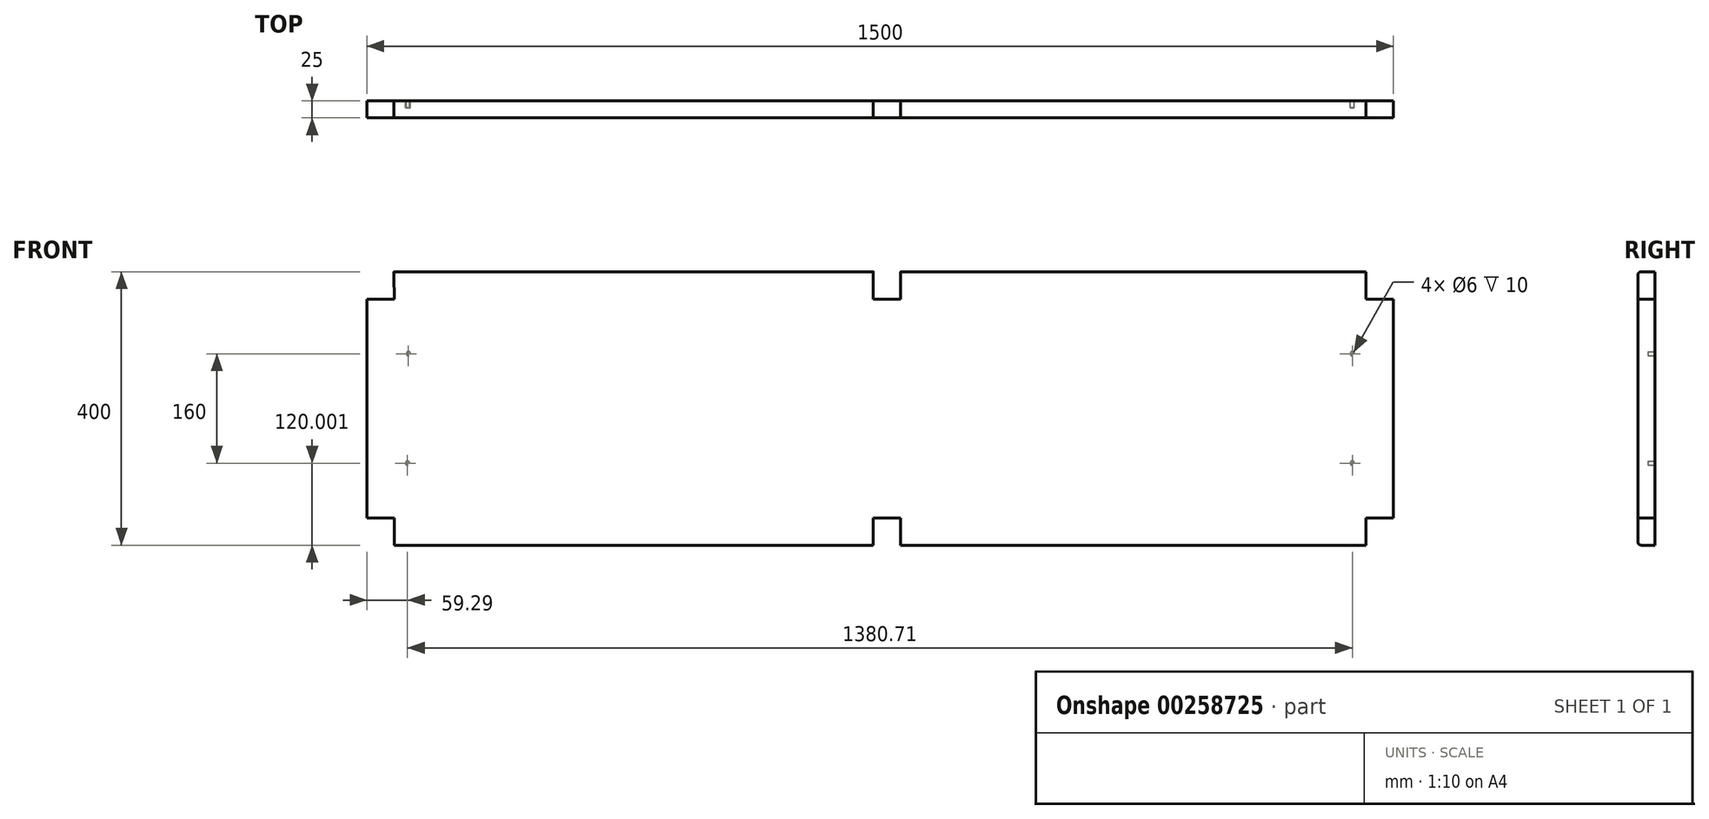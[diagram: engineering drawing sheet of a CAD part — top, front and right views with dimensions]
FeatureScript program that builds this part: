
annotation { "Feature Type Name" : "Feature", "Feature Type Description" : "" }
export const myFeature = defineFeature(function(context is Context, id is Id, definition is map)
    precondition{}
    {
        {
            var Q0;
            Q0=qCreatedBy(makeId("Front.planeOp"),FACE);
            var sketch = newSketch(context, id + "F6", { "sketchPlane" : qUnion([Q0])});
            skLineSegment(sketch, "E0.bottom", {"start": v(1460, -771.13) * mm, "end": v(780, -771.13) * mm});
            skLineSegment(sketch, "E0.top", {"start": v(1460, -371.13) * mm, "end": v(780, -371.13) * mm});
            skLineSegment(sketch, "E0.left", {"start": v(1500, -731.13) * mm, "end": v(1500, -411.13) * mm});
            skLineSegment(sketch, "E0.right", {"start": v(0, -731.13) * mm, "end": v(0, -411.13) * mm});
            skLineSegment(sketch, "E1.top", {"start": v(0, -411.13) * mm, "end": v(40, -411.13) * mm});
            skLineSegment(sketch, "E1.right", {"start": v(39.65, -371.13) * mm, "end": v(40, -411.13) * mm});
            skLineSegment(sketch, "E2.bottom", {"start": v(40, -776.56) * mm, "end": v(40, -776.56) * mm});
            skLineSegment(sketch, "E2.top", {"start": v(40, -776.56) * mm, "end": v(40, -776.56) * mm});
            skLineSegment(sketch, "E2.left", {"start": v(40, -776.56) * mm, "end": v(40, -776.56) * mm});
            skLineSegment(sketch, "E2.right", {"start": v(40, -776.56) * mm, "end": v(40, -776.56) * mm});
            skLineSegment(sketch, "E3.top", {"start": v(0, -731.13) * mm, "end": v(40, -731.13) * mm});
            skLineSegment(sketch, "E3.right", {"start": v(40.36, -771.13) * mm, "end": v(40, -731.13) * mm});
            skLineSegment(sketch, "E4.top", {"start": v(1500, -731.13) * mm, "end": v(1460, -731.13) * mm});
            skLineSegment(sketch, "E4.right", {"start": v(1460, -771.13) * mm, "end": v(1460, -731.13) * mm});
            skLineSegment(sketch, "E5.top", {"start": v(740, -731.13) * mm, "end": v(780, -731.13) * mm});
            skLineSegment(sketch, "E5.left", {"start": v(740, -771.13) * mm, "end": v(740, -731.13) * mm});
            skLineSegment(sketch, "E5.right", {"start": v(780, -771.13) * mm, "end": v(780, -731.13) * mm});
            skLineSegment(sketch, "E6.trimOffspring", {"start": v(740, -771.13) * mm, "end": v(40.36, -771.13) * mm});
            skLineSegment(sketch, "E7.top", {"start": v(740, -411.13) * mm, "end": v(780, -411.13) * mm});
            skLineSegment(sketch, "E7.left", {"start": v(740, -371.13) * mm, "end": v(740, -411.13) * mm});
            skLineSegment(sketch, "E7.right", {"start": v(780, -371.13) * mm, "end": v(780, -411.13) * mm});
            skLineSegment(sketch, "E8.trimOffspring", {"start": v(740, -371.13) * mm, "end": v(39.65, -371.13) * mm});
            skLineSegment(sketch, "E9", {"start": v(1460, -411.13) * mm, "end": v(1500, -411.13) * mm});
            skLineSegment(sketch, "E10", {"start": v(1460, -411.13) * mm, "end": v(1460, -371.13) * mm});
            skSolve(sketch);
        }
        {
            var Q0;
            Q0=makeQuery(id+"F6.imprint","IMPRINT",FACE,{"disambiguationData":[TD([[makeQuery(id+"F6.imprint","IMPRINT",EDGE,{"derivedFrom":sQuery(id+"F6.wireOp",EDGE,"E0.bottom")}),-1.0]])]});
            extrude(context, id + "F0", {"entities" : qUnion([Q0]), "depth" : 25 * mm});
        }
        {
            var Q0;
            Q0=makeQuery(id+"F0.opExtrude","CAP_FACE",FACE,{"disambiguationData":[OSD([sQuery(id+"F6.wireOp",EDGE,"E0.bottom"),sQuery(id+"F6.wireOp",EDGE,"E0.top"),sQuery(id+"F6.wireOp",EDGE,"E0.left"),sQuery(id+"F6.wireOp",EDGE,"E0.right"),sQuery(id+"F6.wireOp",EDGE,"E1.top"),sQuery(id+"F6.wireOp",EDGE,"E1.right"),sQuery(id+"F6.wireOp",EDGE,"E3.top"),sQuery(id+"F6.wireOp",EDGE,"E3.right"),sQuery(id+"F6.wireOp",EDGE,"32319d77-8c54-4927-b478-92323b80e9b3.top"),sQuery(id+"F6.wireOp",EDGE,"32319d77-8c54-4927-b478-92323b80e9b3.right"),sQuery(id+"F6.wireOp",EDGE,"E4.top"),sQuery(id+"F6.wireOp",EDGE,"E4.right"),sQuery(id+"F6.wireOp",EDGE,"E5.top"),sQuery(id+"F6.wireOp",EDGE,"E5.left"),sQuery(id+"F6.wireOp",EDGE,"E5.right"),sQuery(id+"F6.wireOp",EDGE,"E6.trimOffspring"),sQuery(id+"F6.wireOp",EDGE,"E7.top"),sQuery(id+"F6.wireOp",EDGE,"E7.left"),sQuery(id+"F6.wireOp",EDGE,"E7.right"),sQuery(id+"F6.wireOp",EDGE,"E8.trimOffspring")])],"isStart":true});
            var sketch = newSketch(context, id + "F1", { "sketchPlane" : qUnion([Q0])});
            skPoint(sketch, "E11.0", {"position": v(-40, -411.13) * mm});
            skLineSegment(sketch, "E12.0", {"start": v(-39.65, -371.13) * mm, "end": v(-40, -411.13) * mm});
            skLineSegment(sketch, "E13.0", {"start": v(-740, -371.13) * mm, "end": v(-39.65, -371.13) * mm});
            skLineSegment(sketch, "E14.0", {"start": v(-740, -771.13) * mm, "end": v(-40.36, -771.13) * mm});
            skLineSegment(sketch, "E15.0", {"start": v(-40.36, -771.13) * mm, "end": v(-40, -731.13) * mm});
            skCircle(sketch, "E16", {"center": v(-60.72, -491.13) * mm, "radius": 3 * mm});
            skCircle(sketch, "E17", {"center": v(-59.29, -651.13) * mm, "radius": 3 * mm});
            skLineSegment(sketch, "E18.0", {"start": v(-1460, -771.13) * mm, "end": v(-780, -771.13) * mm});
            skPoint(sketch, "E19.0", {"position": v(-1460, -731.13) * mm});
            skLineSegment(sketch, "E20.0", {"start": v(-1460, -771.13) * mm, "end": v(-1460, -731.13) * mm});
            skLineSegment(sketch, "E21.0", {"start": v(-1460, -371.13) * mm, "end": v(-780, -371.13) * mm});
            skCircle(sketch, "E22", {"center": v(-1440, -651.13) * mm, "radius": 3 * mm});
            skCircle(sketch, "E23", {"center": v(-1440, -491.13) * mm, "radius": 3 * mm});
            skSolve(sketch);
        }
        {
            var Q0;
            Q0=makeQuery(id+"F1.imprint","IMPRINT",FACE,{"disambiguationData":[TD([[makeQuery(id+"F1.imprint","IMPRINT",EDGE,{"derivedFrom":sQuery(id+"F1.wireOp",EDGE,"E16")}),1.0]])]});
            extrude(context, id + "F2", {"entities" : qUnion([Q0]), "operationType" : NewBodyOperationType.REMOVE, "oppositeDirection" : true, "depth" : 10 * mm});
        }
        {
            var Q0;
            Q0=makeQuery(id+"F1.imprint","IMPRINT",FACE,{"disambiguationData":[TD([[makeQuery(id+"F1.imprint","IMPRINT",EDGE,{"derivedFrom":sQuery(id+"F1.wireOp",EDGE,"E17")}),1.0]])]});
            var Q1;
            Q1=sQuery(id+"F1.wireOp",EDGE,"E17");
            extrude(context, id + "F7", {"entities" : qUnion([Q0]), "operationType" : NewBodyOperationType.REMOVE, "surfaceEntities" : qUnion([Q1]), "oppositeDirection" : true, "depth" : 10 * mm});
        }
        {
            var Q0;
            Q0 = qSketchRegion(id + "F1", true);
            extrude(context, id + "F3", {"entities" : qUnion([Q0]), "operationType" : NewBodyOperationType.REMOVE, "oppositeDirection" : true, "depth" : 10 * mm});
        }
        {
            var Q0;
            Q0=makeQuery(id+"F0.opExtrude","CAP_EDGE",EDGE,{"disambiguationData":[OSD([sQuery(id+"F6.wireOp",EDGE,"E8.trimOffspring")])],"isStart":false});
            var Q1;
            Q1=makeQuery(id+"F0.opExtrude","CAP_EDGE",EDGE,{"disambiguationData":[OSD([sQuery(id+"F6.wireOp",EDGE,"E6.trimOffspring")])],"isStart":false});
            fillet(context, id + "F4", {"entities" : qUnion([Q0, Q1]), "radius" : 5 * mm, "tangentPropagation" : true, "allowEdgeOverflow" : false});
        }
        {
            var Q0;
            Q0=makeQuery(id+"F0.opExtrude","CAP_EDGE",EDGE,{"disambiguationData":[OSD([sQuery(id+"F6.wireOp",EDGE,"E0.top")])],"isStart":false});
            var Q1;
            Q1=makeQuery(id+"F0.opExtrude","CAP_EDGE",EDGE,{"disambiguationData":[OSD([sQuery(id+"F6.wireOp",EDGE,"E0.bottom")])],"isStart":false});
            fillet(context, id + "F5", {"entities" : qUnion([Q0, Q1]), "radius" : 5 * mm, "tangentPropagation" : true, "allowEdgeOverflow" : false});
        }
    });
